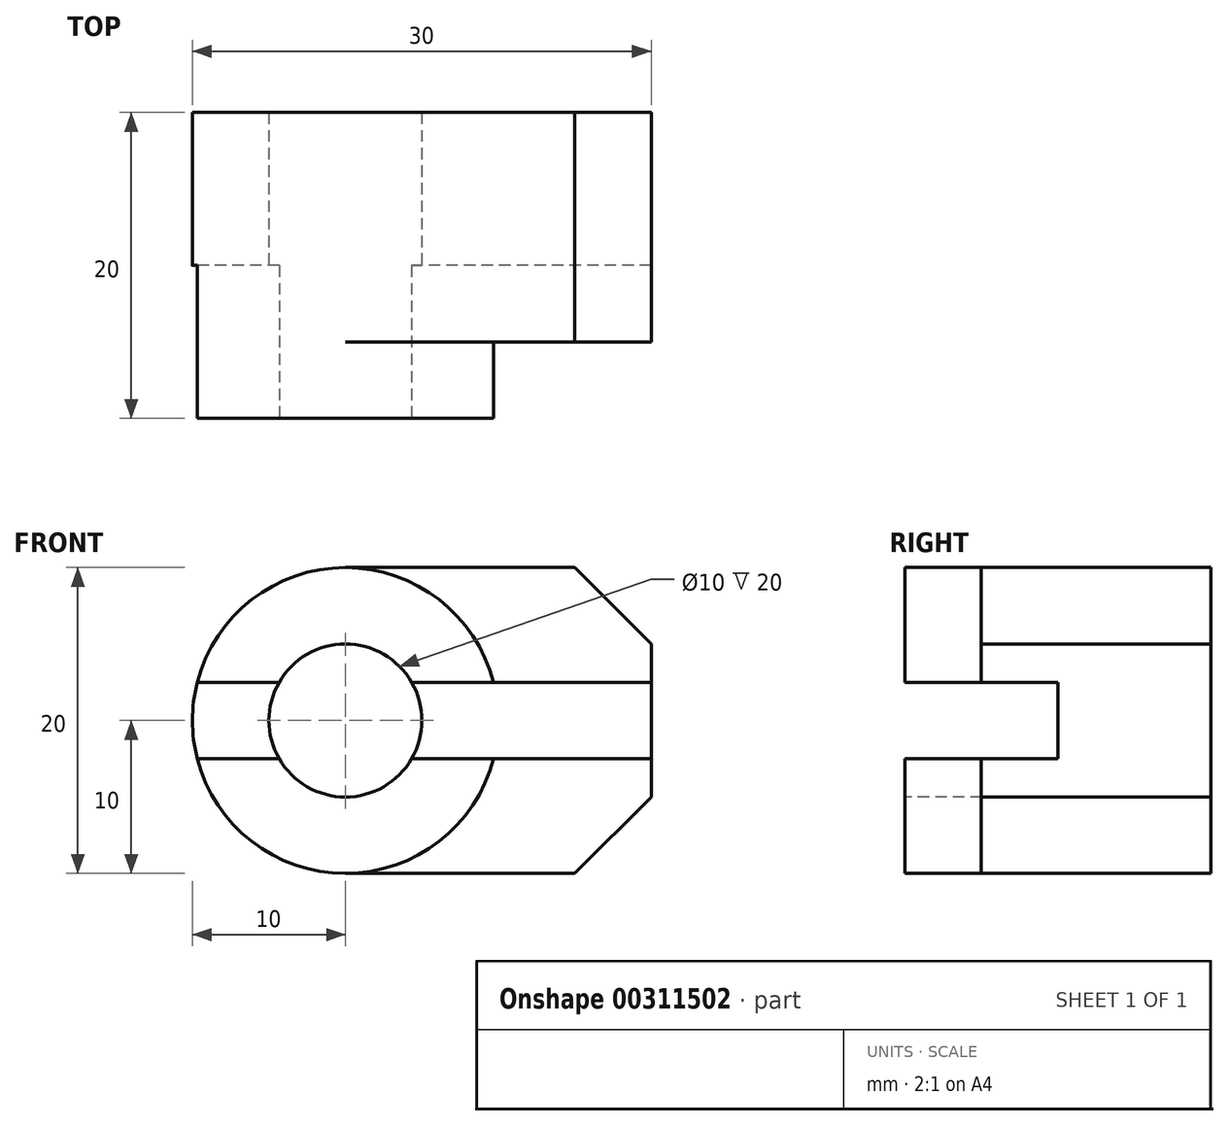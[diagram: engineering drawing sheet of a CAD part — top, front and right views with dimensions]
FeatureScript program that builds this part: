
annotation { "Feature Type Name" : "Feature", "Feature Type Description" : "" }
export const myFeature = defineFeature(function(context is Context, id is Id, definition is map)
    precondition{}
    {
        {
            var Q0;
            Q0=qCreatedBy(makeId("Front.planeOp"),FACE);
            var sketch = newSketch(context, id + "F0", { "sketchPlane" : qUnion([Q0])});
            skLineSegment(sketch, "E0", {"start": v(0, 0) * mm, "end": v(0, 20) * mm, "construction": true});
            skLineSegment(sketch, "E1", {"start": v(0, 20) * mm, "end": v(15, 20) * mm});
            skLineSegment(sketch, "E2", {"start": v(15, 20) * mm, "end": v(20, 15) * mm});
            skLineSegment(sketch, "E3", {"start": v(20, 15) * mm, "end": v(20, 5) * mm});
            skLineSegment(sketch, "E4", {"start": v(20, 5) * mm, "end": v(15, 0) * mm});
            skLineSegment(sketch, "E5", {"start": v(15, 0) * mm, "end": v(0, 0) * mm});
            skArc(sketch, "E6", {"start": v(0, 20) * mm, "mid": v(-10, 10) * mm, "end": v(0, 0) * mm});
            skSolve(sketch);
        }
        {
            var Q0;
            Q0=makeQuery(id+"F0.imprint","IMPRINT",FACE,{"disambiguationData":[TD([[makeQuery(id+"F0.imprint","IMPRINT",EDGE,{"derivedFrom":sQuery(id+"F0.wireOp",EDGE,"E1")}),-1.0]])]});
            extrude(context, id + "F1", {"entities" : qUnion([Q0]), "depth" : 15 * mm});
        }
        {
            var Q0;
            Q0=makeQuery(id+"F1.opExtrude","CAP_FACE",FACE,{"disambiguationData":[OSD([sQuery(id+"F0.wireOp",EDGE,"E1"),sQuery(id+"F0.wireOp",EDGE,"E2"),sQuery(id+"F0.wireOp",EDGE,"E3"),sQuery(id+"F0.wireOp",EDGE,"E4"),sQuery(id+"F0.wireOp",EDGE,"E5"),sQuery(id+"F0.wireOp",EDGE,"E6")])],"isStart":false});
            var sketch = newSketch(context, id + "F2", { "sketchPlane" : qUnion([Q0])});
            skCircle(sketch, "E7", {"center": v(0, 10) * mm, "radius": 10 * mm});
            skSolve(sketch);
        }
        {
            var Q0;
            Q0 = qSketchRegion(id + "F2", true);
            extrude(context, id + "F3", {"entities" : qUnion([Q0]), "operationType" : NewBodyOperationType.ADD, "depth" : 5 * mm});
        }
        {
            var Q0;
            Q0=makeQuery(id+"F3.opExtrude","CAP_FACE",FACE,{"disambiguationData":[OSD([sQuery(id+"F2.wireOp",EDGE,"E7")])],"isStart":false});
            var sketch = newSketch(context, id + "F4", { "sketchPlane" : qUnion([Q0])});
            skCircle(sketch, "E8", {"center": v(0, 10) * mm, "radius": 5 * mm});
            skSolve(sketch);
        }
        {
            var Q0;
            Q0 = qSketchRegion(id + "F4", true);
            extrude(context, id + "F5", {"entities" : qUnion([Q0]), "operationType" : NewBodyOperationType.REMOVE, "endBound" : BoundingType.THROUGH_ALL, "oppositeDirection" : true, "depth" : 25 * mm});
        }
        {
            var Q0;
            Q0=makeQuery(id+"F3.opExtrude","CAP_FACE",FACE,{"disambiguationData":[OSD([sQuery(id+"F2.wireOp",EDGE,"E7")])],"isStart":false});
            var sketch = newSketch(context, id + "F6", { "sketchPlane" : qUnion([Q0])});
            skLineSegment(sketch, "E9", {"start": v(0, 10) * mm, "end": v(0, 12.5) * mm, "construction": true});
            skLineSegment(sketch, "E10", {"start": v(0, 10) * mm, "end": v(0, 7.5) * mm, "construction": true});
            skLineSegment(sketch, "E11", {"start": v(0, 7.5) * mm, "end": v(25, 7.5) * mm});
            skLineSegment(sketch, "E12", {"start": v(25, 7.5) * mm, "end": v(25, 12.5) * mm});
            skLineSegment(sketch, "E13", {"start": v(25, 12.5) * mm, "end": v(0, 12.5) * mm});
            skLineSegment(sketch, "E14", {"start": v(0, 12.5) * mm, "end": v(-15, 12.5) * mm});
            skLineSegment(sketch, "E15", {"start": v(-15, 12.5) * mm, "end": v(-15, 7.5) * mm});
            skLineSegment(sketch, "E16", {"start": v(-15, 7.5) * mm, "end": v(0, 7.5) * mm});
            skSolve(sketch);
        }
        {
            var Q0;
            Q0 = qSketchRegion(id + "F6", true);
            extrude(context, id + "F7", {"entities" : qUnion([Q0]), "operationType" : NewBodyOperationType.REMOVE, "oppositeDirection" : true, "depth" : 10 * mm});
        }
    });
